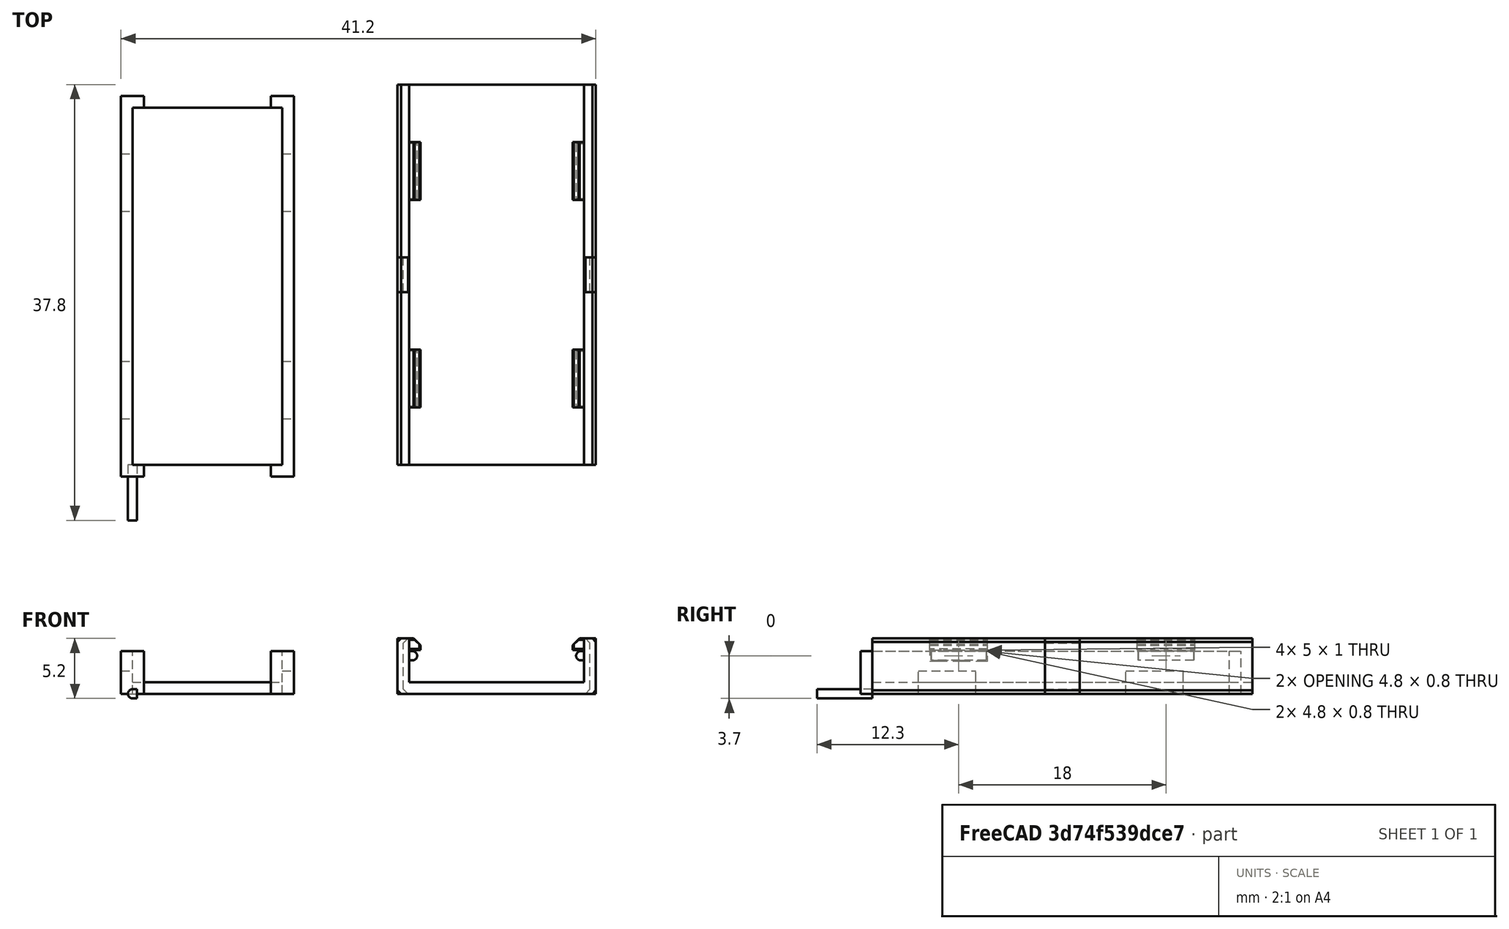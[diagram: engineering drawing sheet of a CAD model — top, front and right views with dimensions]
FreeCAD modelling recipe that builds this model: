
FCSTD DOCUMENT  (FreeCAD 0.17R13541 (Git))
Label: bl-touch-wirebox
License: All rights reserved
LicenseURL: http://en.wikipedia.org/wiki/All_rights_reserved
objects: Part::Box×25, Part::Feature×8, Part::MultiFuse×6, Part::Chamfer×5, Part::Cut×2, Part::Cylinder×1
note: 47 computed .brp shape members not serialized (recipe doc carries the construction recipe); baked Part::Feature solids carry a one-line shape summary decoded from their .brp

FEATURE [Part::Box] Box  label="Cube"
  AttacherType = Attacher::AttachEngine3D
  Height = 1
  Length = 13
  Width = 31
FEATURE [Part::Box] Box001  label="Cube001"
  AttacherType = Attacher::AttachEngine3D
  Height = 3.7
  Length = 1
  Placement = pos=(-1,-1,0) rot=(0,0,1;0rad)
  Width = 33
FEATURE [Part::Box] Box002  label="Cube002"
  AttacherType = Attacher::AttachEngine3D
  Height = 3.7
  Length = 1
  Placement = pos=(13,-1,0) rot=(0,0,1;0rad)
  Width = 33
FEATURE [Part::Box] Box003  label="Cube003"
  AttacherType = Attacher::AttachEngine3D
  Height = 3.7
  Length = 1
  Placement = pos=(0,-1,0) rot=(0,0,1;0rad)
  Width = 1
FEATURE [Part::Box] Box004  label="Cube004"
  AttacherType = Attacher::AttachEngine3D
  Height = 3.7
  Length = 1
  Placement = pos=(12,-1,0) rot=(0,0,1;0rad)
  Width = 1
FEATURE [Part::Box] Box005  label="Cube005"
  AttacherType = Attacher::AttachEngine3D
  Height = 3.7
  Length = 1
  Placement = pos=(0,31,0) rot=(0,0,1;0rad)
  Width = 1
FEATURE [Part::Box] Box006  label="Cube006"
  AttacherType = Attacher::AttachEngine3D
  Height = 3.7
  Length = 1
  Placement = pos=(12,31,0) rot=(0,0,1;0rad)
  Width = 1
FEATURE [Part::Box] Box007  label="Cube007"
  AttacherType = Attacher::AttachEngine3D
  Height = 1
  Length = 17.2
  Placement = pos=(23,0,0) rot=(0,0,1;0rad)
  Width = 33
FEATURE [Part::Box] Box008  label="Cube008"
  AttacherType = Attacher::AttachEngine3D
  Height = 3.8
  Length = 1
  Placement = pos=(23,0,1) rot=(0,0,1;0rad)
  Width = 33
FEATURE [Part::Box] Box009  label="Cube009"
  AttacherType = Attacher::AttachEngine3D
  Height = 3.8
  Length = 1
  Placement = pos=(39.2,0,1) rot=(0,0,1;0rad)
  Width = 33
FEATURE [Part::Box] Box010  label="Cube010"
  AttacherType = Attacher::AttachEngine3D
  Height = 2
  Length = 1
  Placement = pos=(13,4,0) rot=(0,0,1;0rad)
  Width = 5
FEATURE [Part::Box] Box011  label="Cube011"
  AttacherType = Attacher::AttachEngine3D
  Height = 2
  Length = 1
  Placement = pos=(13,22,0) rot=(0,0,1;0rad)
  Width = 5
FEATURE [Part::Box] Box012  label="Cube012"
  AttacherType = Attacher::AttachEngine3D
  Height = 2
  Length = 1
  Placement = pos=(-1,4,0) rot=(0,0,1;0rad)
  Width = 5
FEATURE [Part::Box] Box013  label="Cube013"
  AttacherType = Attacher::AttachEngine3D
  Height = 2
  Length = 1
  Placement = pos=(-1,22,0) rot=(0,0,1;0rad)
  Width = 5
FEATURE [Part::MultiFuse] Fusion001
  Shapes = -> [Box,Box001,Box002,Box004,Box003,Box005,Box006]
FEATURE [Part::Box] Box014  label="Cube014"
  AttacherType = Attacher::AttachEngine3D
  Height = 0.9
  Length = 1
  Placement = pos=(24,5,3.8) rot=(0,0,1;0rad)
  Width = 5
FEATURE [Part::Box] Box015  label="Cube015"
  AttacherType = Attacher::AttachEngine3D
  Height = 0.9
  Length = 1
  Placement = pos=(38.2,5,3.8) rot=(0,0,1;0rad)
  Width = 5
FEATURE [Part::Box] Box016  label="Cube016"
  AttacherType = Attacher::AttachEngine3D
  Height = 0.9
  Length = 1
  Placement = pos=(24,23,3.8) rot=(0,0,1;0rad)
  Width = 5
FEATURE [Part::Box] Box017  label="Cube017"
  AttacherType = Attacher::AttachEngine3D
  Height = 0.9
  Length = 1
  Placement = pos=(38.2,23,3.8) rot=(0,0,1;0rad)
  Width = 5
FEATURE [Part::Chamfer] Chamfer
  Base = -> Box014
  Edges = 1 edges r=0.5: [Edge6]
FEATURE [Part::Chamfer] Chamfer001
  Base = -> Box015
  Edges = 1 edges r=0.5: [Edge2]
FEATURE [Part::Chamfer] Chamfer002
  Base = -> Box016
  Edges = 1 edges r=0.5: [Edge6]
FEATURE [Part::Chamfer] Chamfer003
  Base = -> Box017
  Edges = 1 edges r=0.5: [Edge2]
FEATURE [Part::Feature] Chamfer004_solid  label="Chamfer004 (Solid)"
  shape: bbox 17.2 x 33 x 4.8 mm, 48 faces (baked)
FEATURE [Part::Feature] Cut_solid  label="Cut (Solid)"
  shape: bbox 15 x 33 x 3.7 mm, 56 faces (baked)
FEATURE [Part::Box] Box018  label="Cube018"
  AttacherType = Attacher::AttachEngine3D
  Height = 1
  Length = 1
  Placement = pos=(23,5,2.8) rot=(0,0,1;0rad)
  Width = 5
FEATURE [Part::Box] Box019  label="Cube019"
  AttacherType = Attacher::AttachEngine3D
  Height = 1
  Length = 1
  Placement = pos=(23,23,2.8) rot=(0,0,1;0rad)
  Width = 5
FEATURE [Part::Box] Box020  label="Cube020"
  AttacherType = Attacher::AttachEngine3D
  Height = 1
  Length = 1
  Placement = pos=(39.2,5,2.8) rot=(0,0,1;0rad)
  Width = 5
FEATURE [Part::Box] Box021  label="Cube021"
  AttacherType = Attacher::AttachEngine3D
  Height = 1
  Length = 1
  Placement = pos=(39.2,23,2.8) rot=(0,0,1;0rad)
  Width = 5
FEATURE [Part::MultiFuse] Fusion002
  Shapes = -> [Box021,Box020,Box019,Box018,Box007,Box008,Box009]
FEATURE [Part::Cylinder] Cylinder
  Angle = 360
  AttacherType = Attacher::AttachEngine3D
  Height = 4.8
  Radius = 0.4
FEATURE [Part::Box] Box022  label="Cube022"
  AttacherType = Attacher::AttachEngine3D
  Height = 4.8
  Length = 0.8
  Placement = pos=(-0.4,0,0) rot=(0,0,1;0rad)
  Width = 0.4
FEATURE [Part::MultiFuse] Fusion003
  Placement = pos=(0,0,0) rot=(-0.57735,-0.57735,0.57735;4.18879rad)
  Shapes = -> [Box022,Cylinder]
FEATURE [Part::Feature] Fusion003001  label="Fusion004"
  Placement = pos=(24.3,5.1,3.3) rot=(-0.57735,0.57735,0.57735;2.0944rad)
  shape: bbox 0.8 x 4.8 x 0.8 mm, 13 faces (baked)
FEATURE [Part::Feature] Fusion003002  label="Fusion005"
  Placement = pos=(24.3,23.1,3.3) rot=(-0.57735,0.57735,0.57735;2.0944rad)
  shape: bbox 0.8 x 4.8 x 0.8 mm, 13 faces (baked)
FEATURE [Part::Feature] Fusion003003  label="Fusion006"
  Placement = pos=(38.9,9.9,3.3) rot=(0.57735,0.57735,-0.57735;2.0944rad)
  shape: bbox 0.8 x 4.8 x 0.8 mm, 13 faces (baked)
FEATURE [Part::Feature] Fusion003004  label="Fusion007"
  Placement = pos=(38.9,27.9,3.3) rot=(-0.57735,-0.57735,0.57735;4.18879rad)
  shape: bbox 0.8 x 4.8 x 0.8 mm, 13 faces (baked)
FEATURE [Part::MultiFuse] Fusion003005
  Shapes = -> [Fusion003004,Fusion003003,Fusion003002,Fusion003001,Fusion002]
FEATURE [Part::Box] Box023  label="Cube023"
  AttacherType = Attacher::AttachEngine3D
  Height = 9
  Length = 0.5
  Placement = pos=(39.7,15,0) rot=(0,0,1;0rad)
  Width = 3
FEATURE [Part::Box] Box024  label="Cube024"
  AttacherType = Attacher::AttachEngine3D
  Height = 9
  Length = 0.5
  Placement = pos=(23,15,0) rot=(0,0,1;0rad)
  Width = 3
FEATURE [Part::MultiFuse] Fusion003006
  Shapes = -> [Box024,Box023]
FEATURE [Part::Cut] Cut001
  Base = -> Fusion003005
  Tool = -> Fusion003006
FEATURE [Part::Chamfer] Chamfer004  label="outer"
  Base = -> Cut001
  Edges = 4 edges r=0.4: [Edge41,Edge77,Edge109,Edge120]
FEATURE [Part::MultiFuse] Fusion
  Shapes = -> [Box013,Box012,Box011,Box010]
FEATURE [Part::Cut] Cut  label="inner"
  Base = -> Fusion001
  Tool = -> Fusion
FEATURE [Part::Feature] Cut002  label="inner001"
  shape: bbox 15 x 33 x 3.7 mm, 38 faces (baked)
FEATURE [Part::Feature] Chamfer004001  label="outer001"
  shape: bbox 17.2 x 33 x 4.8 mm, 42 faces (baked)
